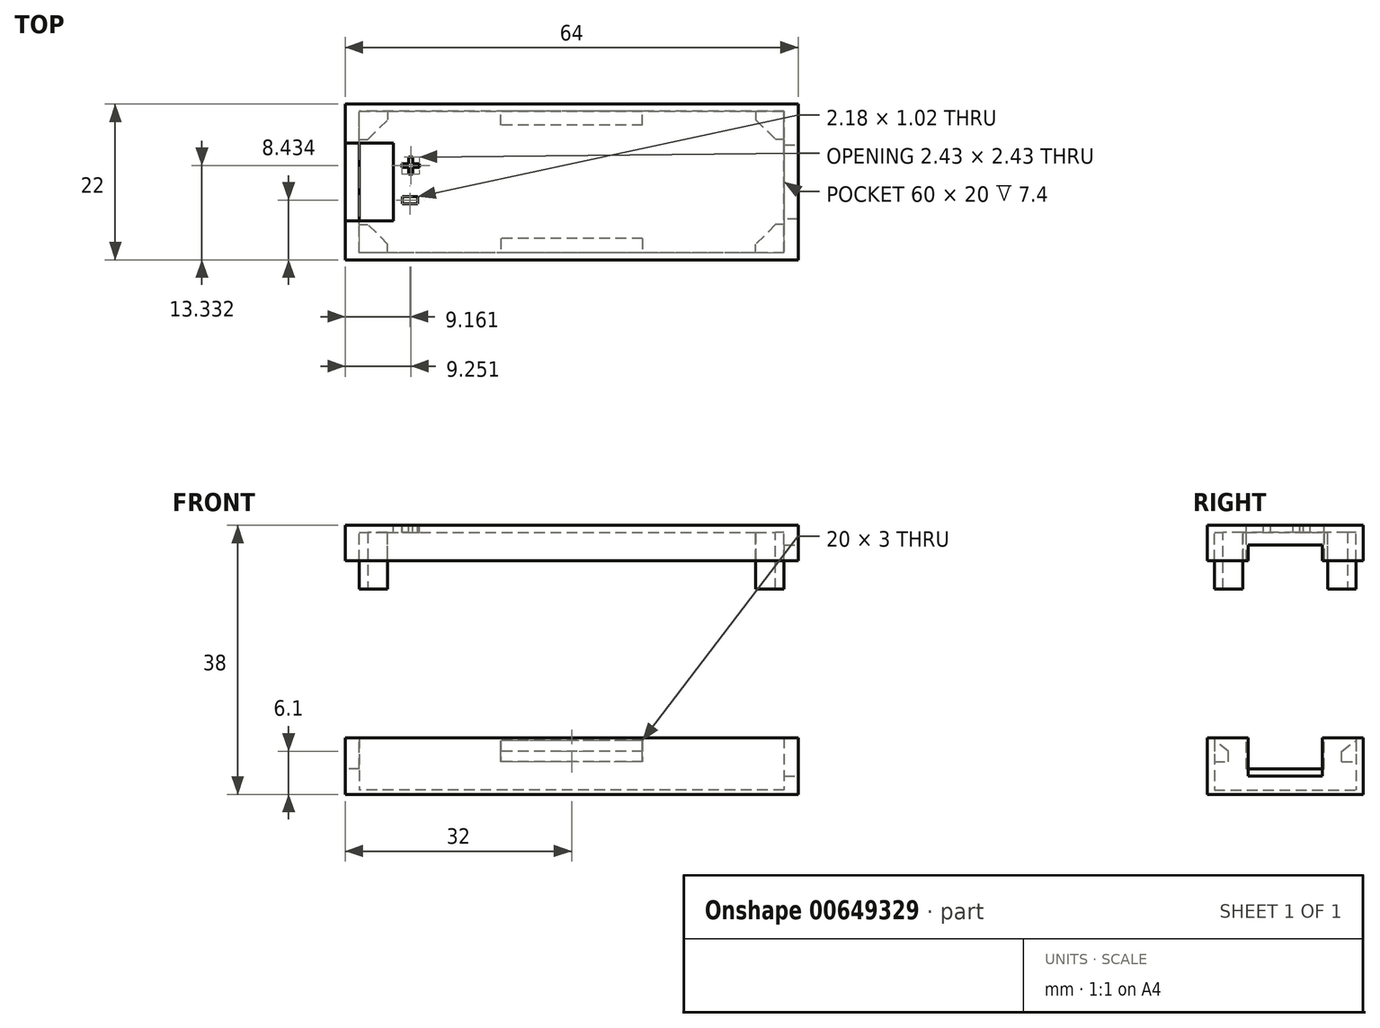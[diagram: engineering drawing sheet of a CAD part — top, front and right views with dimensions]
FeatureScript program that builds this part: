
annotation { "Feature Type Name" : "Feature", "Feature Type Description" : "" }
export const myFeature = defineFeature(function(context is Context, id is Id, definition is map)
    precondition{}
    {
        {
            var Q0;
            Q0=qCreatedBy(makeId("Top.planeOp"),FACE);
            var sketch = newSketch(context, id + "F0", { "sketchPlane" : qUnion([Q0])});
            skLineSegment(sketch, "E0.bottom", {"start": v(0, 0) * mm, "end": v(-60, 0) * mm});
            skLineSegment(sketch, "E0.top", {"start": v(0, 20) * mm, "end": v(-60, 20) * mm});
            skLineSegment(sketch, "E0.left", {"start": v(0, 0) * mm, "end": v(0, 20) * mm});
            skLineSegment(sketch, "E0.right", {"start": v(-60, 0) * mm, "end": v(-60, 20) * mm});
            skLineSegment(sketch, "E1.bottom", {"start": v(2, -1) * mm, "end": v(-62, -1) * mm});
            skLineSegment(sketch, "E1.top", {"start": v(2, 21) * mm, "end": v(-62, 21) * mm});
            skLineSegment(sketch, "E1.left", {"start": v(2, -1) * mm, "end": v(2, 21) * mm});
            skLineSegment(sketch, "E1.right", {"start": v(-62, -1) * mm, "end": v(-62, 21) * mm});
            skSolve(sketch);
        }
        {
            var Q0;
            Q0=makeQuery(id+"F0.imprint","IMPRINT",FACE,{"disambiguationData":[TD([[makeQuery(id+"F0.imprint","IMPRINT",EDGE,{"derivedFrom":sQuery(id+"F0.wireOp",EDGE,"E0.bottom")}),-1.0]])]});
            extrude(context, id + "F1", {"entities" : qUnion([Q0]), "depth" : .6 * mm, "offsetDistance" : 25 * mm});
        }
        {
            var Q0;
            Q0=makeQuery(id+"F0.imprint","IMPRINT",FACE,{"disambiguationData":[TD([[makeQuery(id+"F0.imprint","IMPRINT",EDGE,{"derivedFrom":sQuery(id+"F0.wireOp",EDGE,"E0.bottom")}),1.0]])]});
            extrude(context, id + "F2", {"entities" : qUnion([Q0]), "operationType" : NewBodyOperationType.ADD, "depth" : 8 * mm, "offsetDistance" : 25 * mm});
        }
        {
            var Q0;
            Q0=makeQuery(id+"F2.opExtrude","CAP_EDGE",EDGE,{"disambiguationData":[OSD([sQuery(id+"F0.wireOp",EDGE,"E0.top")])],"isStart":false});
            cPoint(context, id + "F3", {"entities" : qUnion([Q0]), "parameter" : 0.5});
        }
        {
            var Q0;
            Q0 = qCreatedBy(id + "F3" ,VERTEX);
            var Q1;
            Q1=makeQuery(id+"F2.opExtrude","SWEPT_FACE",FACE,{"disambiguationData":[OSD([sQuery(id+"F0.wireOp",EDGE,"E0.right")])]});
            cPlane(context, id + "F4", {"entities" : qUnion([Q0, Q1]), "cplaneType" : CPlaneType.PLANE_POINT, "offset" : 25 * mm, "width" : 150 * mm, "height" : 150 * mm});
        }
        {
            var Q0;
            Q0=qCreatedBy(id+"F4.planeOp",FACE);
            var sketch = newSketch(context, id + "F5", { "sketchPlane" : qUnion([Q0])});
            skLineSegment(sketch, "E2", {"start": v(20, 7.6) * mm, "end": v(20, 4.6) * mm});
            skLineSegment(sketch, "E3", {"start": v(18, 4.6) * mm, "end": v(20, 4.6) * mm});
            skLineSegment(sketch, "E4", {"start": v(0, 7.6) * mm, "end": v(0, 4.6) * mm});
            skLineSegment(sketch, "E5", {"start": v(0, 4.6) * mm, "end": v(2, 4.6) * mm});
            skLineSegment(sketch, "E6.0", {"start": v(0, 8) * mm, "end": v(0, 0.6) * mm, "construction": true});
            skLineSegment(sketch, "E6.1", {"start": v(20, 8) * mm, "end": v(20, 0.6) * mm, "construction": true});
            skLineSegment(sketch, "E7", {"start": v(18, 4.6) * mm, "end": v(18, 6.1) * mm});
            skLineSegment(sketch, "E8", {"start": v(18, 6.1) * mm, "end": v(20, 7.6) * mm});
            skLineSegment(sketch, "E9", {"start": v(2, 4.6) * mm, "end": v(2, 6.1) * mm});
            skLineSegment(sketch, "E10", {"start": v(2, 6.1) * mm, "end": v(0, 7.6) * mm});
            skSolve(sketch);
        }
        {
            var Q0;
            Q0=makeQuery(id+"F5.imprint","IMPRINT",FACE,{"disambiguationData":[TD([[makeQuery(id+"F5.imprint","IMPRINT",EDGE,{"derivedFrom":sQuery(id+"F5.wireOp",EDGE,"E4")}),1.0]])]});
            var Q1;
            Q1=makeQuery(id+"F5.imprint","IMPRINT",FACE,{"disambiguationData":[TD([[makeQuery(id+"F5.imprint","IMPRINT",EDGE,{"derivedFrom":sQuery(id+"F5.wireOp",EDGE,"E2")}),-1.0]])]});
            extrude(context, id + "F6", {"entities" : qUnion([Q0, Q1]), "operationType" : NewBodyOperationType.ADD, "endBound" : BoundingType.SYMMETRIC, "depth" : 20 * mm, "offsetDistance" : 25 * mm});
        }
        {
            var Q0;
            Q0=makeQuery(id+"F2.opExtrude","SWEPT_FACE",FACE,{"disambiguationData":[OSD([sQuery(id+"F0.wireOp",EDGE,"E1.left")])]});
            var sketch = newSketch(context, id + "F7", { "sketchPlane" : qUnion([Q0])});
            skLineSegment(sketch, "E11.bottom", {"start": v(4.75, 8) * mm, "end": v(15.25, 8) * mm});
            skLineSegment(sketch, "E11.top", {"start": v(4.75, 2.6) * mm, "end": v(15.25, 2.6) * mm});
            skLineSegment(sketch, "E11.left", {"start": v(4.75, 8) * mm, "end": v(4.75, 2.6) * mm});
            skLineSegment(sketch, "E11.right", {"start": v(15.25, 8) * mm, "end": v(15.25, 2.6) * mm});
            skLineSegment(sketch, "E12", {"start": v(10, 8) * mm, "end": v(10, 2.6) * mm, "construction": true});
            skSolve(sketch);
        }
        {
            var Q0;
            Q0=makeQuery(id+"F7.imprint","IMPRINT",FACE,{"disambiguationData":[TD([[makeQuery(id+"F7.imprint","IMPRINT",EDGE,{"derivedFrom":sQuery(id+"F7.wireOp",EDGE,"E11.bottom")}),-1.0]])]});
            extrude(context, id + "F8", {"entities" : qUnion([Q0]), "operationType" : NewBodyOperationType.REMOVE, "endBound" : BoundingType.UP_TO_NEXT, "oppositeDirection" : true, "depth" : 25 * mm, "offsetDistance" : 25 * mm});
        }
        {
            var Q0;
            Q0=makeQuery(id+"F2.opExtrude","SWEPT_FACE",FACE,{"disambiguationData":[OSD([sQuery(id+"F0.wireOp",EDGE,"E1.right")])]});
            var sketch = newSketch(context, id + "F9", { "sketchPlane" : qUnion([Q0])});
            skLineSegment(sketch, "E13.bottom", {"start": v(-15.5, 8) * mm, "end": v(-4.5, 8) * mm});
            skLineSegment(sketch, "E13.top", {"start": v(-15.5, 3.6) * mm, "end": v(-4.5, 3.6) * mm});
            skLineSegment(sketch, "E13.left", {"start": v(-15.5, 8) * mm, "end": v(-15.5, 3.6) * mm});
            skLineSegment(sketch, "E13.right", {"start": v(-4.5, 8) * mm, "end": v(-4.5, 3.6) * mm});
            skLineSegment(sketch, "E14", {"start": v(-10, 8) * mm, "end": v(-10, 3.6) * mm, "construction": true});
            skSolve(sketch);
        }
        {
            var Q0;
            Q0=makeQuery(id+"F9.imprint","IMPRINT",FACE,{"disambiguationData":[TD([[makeQuery(id+"F9.imprint","IMPRINT",EDGE,{"derivedFrom":sQuery(id+"F9.wireOp",EDGE,"E13.bottom")}),1.0]])]});
            extrude(context, id + "F10", {"entities" : qUnion([Q0]), "operationType" : NewBodyOperationType.REMOVE, "endBound" : BoundingType.UP_TO_NEXT, "oppositeDirection" : true, "depth" : 25 * mm, "offsetDistance" : 25 * mm});
        }
        {
            var Q0;
            {var subQ0=sQuery(id+"F0.wireOp",EDGE,"E1.bottom");var subQ1=sQuery(id+"F0.wireOp",EDGE,"E0.left");var subQ2=sQuery(id+"F0.wireOp",EDGE,"E0.right");var subQ3=sQuery(id+"F0.wireOp",EDGE,"E0.bottom");var subQ4=sQuery(id+"F0.wireOp",EDGE,"E1.left");var subQ5=sQuery(id+"F0.wireOp",EDGE,"E1.right");Q0=makeQuery(id+"F10.boolean.opBoolean","SPLIT",FACE,{"disambiguationData":[TD([makeQuery(id+"F2.opExtrude","SWEPT_FACE",FACE,{"disambiguationData":[OSD([subQ3])]})])],"derivedFrom":makeQuery(id+"F2.opExtrude","CAP_FACE",FACE,{"disambiguationData":[OSD([subQ3,sQuery(id+"F0.wireOp",EDGE,"E0.top"),subQ1,subQ2,subQ0,sQuery(id+"F0.wireOp",EDGE,"E1.top"),subQ4,subQ5])],"isStart":false})});}
            cPlane(context, id + "F11", {"entities" : qUnion([Q0]), "cplaneType" : CPlaneType.OFFSET, "offset" : 25 * mm, "width" : 150 * mm, "height" : 150 * mm});
        }
        {
            var Q0;
            Q0=qCreatedBy(id+"F11.planeOp",FACE);
            var sketch = newSketch(context, id + "F12", { "sketchPlane" : qUnion([Q0])});
            skLineSegment(sketch, "E15.0.0", {"start": v(-62, 15.5) * mm, "end": v(-60, 15.5) * mm});
            skLineSegment(sketch, "E15.0.1", {"start": v(-60, 15.5) * mm, "end": v(-60, 20) * mm});
            skLineSegment(sketch, "E15.0.2", {"start": v(-60, 20) * mm, "end": v(0, 20) * mm});
            skLineSegment(sketch, "E15.0.3", {"start": v(0, 20) * mm, "end": v(0, 15.25) * mm});
            skLineSegment(sketch, "E15.0.4", {"start": v(0, 15.25) * mm, "end": v(2, 15.25) * mm});
            skLineSegment(sketch, "E15.0.5", {"start": v(2, 15.25) * mm, "end": v(2, 21) * mm});
            skLineSegment(sketch, "E15.0.6", {"start": v(2, 21) * mm, "end": v(-62, 21) * mm});
            skLineSegment(sketch, "E15.0.7", {"start": v(-62, 21) * mm, "end": v(-62, 15.5) * mm});
            skLineSegment(sketch, "E15.1.0", {"start": v(-60, 0) * mm, "end": v(-60, 4.5) * mm});
            skLineSegment(sketch, "E15.1.1", {"start": v(-60, 4.5) * mm, "end": v(-62, 4.5) * mm});
            skLineSegment(sketch, "E15.1.2", {"start": v(-62, 4.5) * mm, "end": v(-62, -1) * mm});
            skLineSegment(sketch, "E15.1.3", {"start": v(-62, -1) * mm, "end": v(2, -1) * mm});
            skLineSegment(sketch, "E15.1.4", {"start": v(2, -1) * mm, "end": v(2, 4.75) * mm});
            skLineSegment(sketch, "E15.1.5", {"start": v(2, 4.75) * mm, "end": v(0, 4.75) * mm});
            skLineSegment(sketch, "E15.1.6", {"start": v(0, 4.75) * mm, "end": v(0, 0) * mm});
            skLineSegment(sketch, "E15.1.7", {"start": v(0, 0) * mm, "end": v(-60, 0) * mm});
            skLineSegment(sketch, "E16", {"start": v(-62, 15.5) * mm, "end": v(-62, 4.5) * mm});
            skLineSegment(sketch, "E17", {"start": v(-60, 4.5) * mm, "end": v(-60, 15.5) * mm});
            skLineSegment(sketch, "E18", {"start": v(0, 15.25) * mm, "end": v(0, 4.75) * mm});
            skLineSegment(sketch, "E19", {"start": v(2, 4.75) * mm, "end": v(2, 15.25) * mm});
            skSolve(sketch);
        }
        {
            var Q0;
            Q0=makeQuery(id+"F12.imprint","IMPRINT",FACE,{"disambiguationData":[TD([[makeQuery(id+"F12.imprint","IMPRINT",EDGE,{"derivedFrom":sQuery(id+"F12.wireOp",EDGE,"E15.0.0")}),1.0]])]});
            var Q1;
            Q1=makeQuery(id+"F12.imprint","IMPRINT",FACE,{"disambiguationData":[TD([[makeQuery(id+"F12.imprint","IMPRINT",EDGE,{"derivedFrom":sQuery(id+"F12.wireOp",EDGE,"E15.0.0")}),-1.0]])]});
            var Q2;
            Q2=makeQuery(id+"F12.imprint","IMPRINT",FACE,{"disambiguationData":[TD([[makeQuery(id+"F12.imprint","IMPRINT",EDGE,{"derivedFrom":sQuery(id+"F12.wireOp",EDGE,"E15.1.0")}),1.0]])]});
            var Q3;
            Q3=makeQuery(id+"F12.imprint","IMPRINT",FACE,{"disambiguationData":[TD([[makeQuery(id+"F12.imprint","IMPRINT",EDGE,{"derivedFrom":sQuery(id+"F12.wireOp",EDGE,"E15.0.4")}),-1.0]])]});
            extrude(context, id + "F13", {"entities" : qUnion([Q0, Q1, Q2, Q3]), "depth" : 4 * mm, "offsetDistance" : 25 * mm});
        }
        {
            var Q0;
            Q0=makeQuery(id+"F13.opExtrude","CAP_FACE",FACE,{"disambiguationData":[OSD([sQuery(id+"F12.wireOp",EDGE,"E15.0.1"),sQuery(id+"F12.wireOp",EDGE,"E15.0.2"),sQuery(id+"F12.wireOp",EDGE,"E15.0.3"),sQuery(id+"F12.wireOp",EDGE,"E15.0.5"),sQuery(id+"F12.wireOp",EDGE,"E15.0.6"),sQuery(id+"F12.wireOp",EDGE,"E15.0.7"),sQuery(id+"F12.wireOp",EDGE,"E15.1.0"),sQuery(id+"F12.wireOp",EDGE,"E15.1.2"),sQuery(id+"F12.wireOp",EDGE,"E15.1.3"),sQuery(id+"F12.wireOp",EDGE,"E15.1.4"),sQuery(id+"F12.wireOp",EDGE,"E15.1.6"),sQuery(id+"F12.wireOp",EDGE,"E15.1.7"),sQuery(id+"F12.wireOp",EDGE,"E16"),sQuery(id+"F12.wireOp",EDGE,"E17"),sQuery(id+"F12.wireOp",EDGE,"E18"),sQuery(id+"F12.wireOp",EDGE,"E19")])],"isStart":false});
            var sketch = newSketch(context, id + "F14", { "sketchPlane" : qUnion([Q0])});
            skLineSegment(sketch, "E20.bottom", {"start": v(-62, 21) * mm, "end": v(2, 21) * mm});
            skLineSegment(sketch, "E20.top", {"start": v(-62, -1) * mm, "end": v(2, -1) * mm});
            skLineSegment(sketch, "E20.left", {"start": v(-62, 21) * mm, "end": v(-62, -1) * mm});
            skLineSegment(sketch, "E20.right", {"start": v(2, 21) * mm, "end": v(2, -1) * mm});
            skSolve(sketch);
        }
        {
            var Q0;
            Q0 = qSketchRegion(id + "F14", true);
            extrude(context, id + "F15", {"entities" : qUnion([Q0]), "operationType" : NewBodyOperationType.ADD, "depth" : 1 * mm, "offsetDistance" : 25 * mm});
        }
        {
            var Q0;
            Q0=makeQuery(id+"F12.imprint","IMPRINT",FACE,{"disambiguationData":[TD([[makeQuery(id+"F12.imprint","IMPRINT",EDGE,{"derivedFrom":sQuery(id+"F12.wireOp",EDGE,"E15.0.4")}),-1.0]])]});
            extrude(context, id + "F16", {"entities" : qUnion([Q0]), "operationType" : NewBodyOperationType.REMOVE, "depth" : 2.2 * mm, "offsetDistance" : 25 * mm});
        }
        {
            var Q0;
            Q0=makeQuery(id+"F15.opExtrude","CAP_FACE",FACE,{"disambiguationData":[OSD([sQuery(id+"F14.wireOp",EDGE,"E20.bottom"),sQuery(id+"F14.wireOp",EDGE,"E20.top"),sQuery(id+"F14.wireOp",EDGE,"E20.left"),sQuery(id+"F14.wireOp",EDGE,"E20.right")])],"isStart":false});
            var sketch = newSketch(context, id + "F17", { "sketchPlane" : qUnion([Q0])});
            skPoint(sketch, "E21.0", {"position": v(-62, 4.5) * mm});
            skPoint(sketch, "E21.1", {"position": v(-62, 15.5) * mm});
            skLineSegment(sketch, "E22", {"start": v(-62, 4.5) * mm, "end": v(-62, 15.5) * mm});
            skLineSegment(sketch, "E23", {"start": v(-55.2, 15.5) * mm, "end": v(-55.2, 4.5) * mm});
            skLineSegment(sketch, "E24", {"start": v(-55.2, 4.5) * mm, "end": v(-62, 4.5) * mm});
            skLineSegment(sketch, "E25", {"start": v(-62, 15.5) * mm, "end": v(-55.2, 15.5) * mm});
            skSolve(sketch);
        }
        {
            var Q0;
            Q0=makeQuery(id+"F17.imprint","IMPRINT",FACE,{"disambiguationData":[TD([[makeQuery(id+"F17.imprint","IMPRINT",EDGE,{"derivedFrom":sQuery(id+"F17.wireOp",EDGE,"E22")}),1.0]])]});
            extrude(context, id + "F18", {"entities" : qUnion([Q0]), "operationType" : NewBodyOperationType.REMOVE, "endBound" : BoundingType.UP_TO_NEXT, "oppositeDirection" : true, "depth" : 25 * mm, "offsetDistance" : 25 * mm});
        }
        {
            var Q0;
            Q0=makeQuery(id+"F15.opExtrude","CAP_FACE",FACE,{"disambiguationData":[OSD([sQuery(id+"F14.wireOp",EDGE,"E20.bottom"),sQuery(id+"F14.wireOp",EDGE,"E20.top"),sQuery(id+"F14.wireOp",EDGE,"E20.left"),sQuery(id+"F14.wireOp",EDGE,"E20.right")])],"isStart":true});
            var sketch = newSketch(context, id + "F19", { "sketchPlane" : qUnion([Q0])});
            skLineSegment(sketch, "E26.bottom", {"start": v(-60, 0) * mm, "end": v(-56, 0) * mm});
            skLineSegment(sketch, "E26.top", {"start": v(-60, -4) * mm, "end": v(-56, -4) * mm});
            skLineSegment(sketch, "E26.left", {"start": v(-60, 0) * mm, "end": v(-60, -4) * mm});
            skLineSegment(sketch, "E26.right", {"start": v(-56, 0) * mm, "end": v(-56, -4) * mm});
            skLineSegment(sketch, "E27.bottom", {"start": v(-60, -20) * mm, "end": v(-56, -20) * mm});
            skLineSegment(sketch, "E27.top", {"start": v(-60, -16) * mm, "end": v(-56, -16) * mm});
            skLineSegment(sketch, "E27.left", {"start": v(-60, -20) * mm, "end": v(-60, -16) * mm});
            skLineSegment(sketch, "E27.right", {"start": v(-56, -20) * mm, "end": v(-56, -16) * mm});
            skLineSegment(sketch, "E28.bottom", {"start": v(0, 0) * mm, "end": v(-4, 0) * mm});
            skLineSegment(sketch, "E28.top", {"start": v(0, -4) * mm, "end": v(-4, -4) * mm});
            skLineSegment(sketch, "E28.left", {"start": v(0, 0) * mm, "end": v(0, -4) * mm});
            skLineSegment(sketch, "E28.right", {"start": v(-4, 0) * mm, "end": v(-4, -4) * mm});
            skLineSegment(sketch, "E29.bottom", {"start": v(0, -20) * mm, "end": v(-4, -20) * mm});
            skLineSegment(sketch, "E29.top", {"start": v(0, -16) * mm, "end": v(-4, -16) * mm});
            skLineSegment(sketch, "E29.left", {"start": v(0, -20) * mm, "end": v(0, -16) * mm});
            skLineSegment(sketch, "E29.right", {"start": v(-4, -20) * mm, "end": v(-4, -16) * mm});
            skSolve(sketch);
        }
        {
            var Q0;
            Q0=makeQuery(id+"F19.imprint","IMPRINT",FACE,{"disambiguationData":[TD([[makeQuery(id+"F19.imprint","IMPRINT",EDGE,{"derivedFrom":sQuery(id+"F19.wireOp",EDGE,"E29.bottom")}),1.0]])]});
            var Q1;
            Q1=makeQuery(id+"F19.imprint","IMPRINT",FACE,{"disambiguationData":[TD([[makeQuery(id+"F19.imprint","IMPRINT",EDGE,{"derivedFrom":sQuery(id+"F19.wireOp",EDGE,"E28.bottom")}),1.0]])]});
            var Q2;
            Q2=makeQuery(id+"F19.imprint","IMPRINT",FACE,{"disambiguationData":[TD([[makeQuery(id+"F19.imprint","IMPRINT",EDGE,{"derivedFrom":sQuery(id+"F19.wireOp",EDGE,"E26.bottom")}),1.0]])]});
            var Q3;
            Q3=makeQuery(id+"F19.imprint","IMPRINT",FACE,{"disambiguationData":[TD([[makeQuery(id+"F19.imprint","IMPRINT",EDGE,{"derivedFrom":sQuery(id+"F19.wireOp",EDGE,"E27.bottom")}),1.0]])]});
            extrude(context, id + "F20", {"entities" : qUnion([Q0, Q1, Q2, Q3]), "operationType" : NewBodyOperationType.ADD, "depth" : 8 * mm, "offsetDistance" : 25 * mm});
        }
        {
            var Q0;
            Q0=makeQuery(id+"F20.opExtrude","SWEPT_EDGE",EDGE,{"disambiguationData":[OSD([sQuery(id+"F19.wireOp",EDGE,"E26.top"),sQuery(id+"F19.wireOp",EDGE,"E26.right")])]});
            var Q1;
            Q1=makeQuery(id+"F20.opExtrude","SWEPT_EDGE",EDGE,{"disambiguationData":[OSD([sQuery(id+"F19.wireOp",EDGE,"E27.top"),sQuery(id+"F19.wireOp",EDGE,"E27.right")])]});
            var Q2;
            Q2=makeQuery(id+"F20.opExtrude","SWEPT_EDGE",EDGE,{"disambiguationData":[OSD([sQuery(id+"F19.wireOp",EDGE,"E28.top"),sQuery(id+"F19.wireOp",EDGE,"E28.right")])]});
            var Q3;
            Q3=makeQuery(id+"F20.opExtrude","SWEPT_EDGE",EDGE,{"disambiguationData":[OSD([sQuery(id+"F19.wireOp",EDGE,"E29.top"),sQuery(id+"F19.wireOp",EDGE,"E29.right")])]});
            chamfer(context, id + "F21", {"entities" : qUnion([Q0, Q1, Q2, Q3]), "width" : 2.8 * mm, "tangentPropagation" : true});
        }
        {
            var Q0;
            Q0=makeQuery(id+"F15.opExtrude","CAP_FACE",FACE,{"disambiguationData":[OSD([sQuery(id+"F14.wireOp",EDGE,"E20.bottom"),sQuery(id+"F14.wireOp",EDGE,"E20.top"),sQuery(id+"F14.wireOp",EDGE,"E20.left"),sQuery(id+"F14.wireOp",EDGE,"E20.right")])],"isStart":false});
            var sketch = newSketch(context, id + "F22", { "sketchPlane" : qUnion([Q0])});
            skText(sketch, "E30", { "text": "+", "fontName": "OpenSans-Bold.ttf"});
            skText(sketch, "E31", { "text": "-", "fontName": "OpenSans-Bold.ttf"});
            const initialGuessF22  = {"E30": [-0.05418, 0.01056, 1, 0, 0.00361], "E31": [-0.05418, 0.0052, 1, 0, 0.006]};
            skSetInitialGuess(sketch, initialGuessF22);
            skSolve(sketch);
        }
        {
            var Q0;
            Q0 = qSketchRegion(id + "F22", true);
            extrude(context, id + "F23", {"entities" : qUnion([Q0]), "operationType" : NewBodyOperationType.REMOVE, "endBound" : BoundingType.UP_TO_NEXT, "oppositeDirection" : true, "depth" : 25 * mm, "offsetDistance" : 25 * mm});
        }
    });
